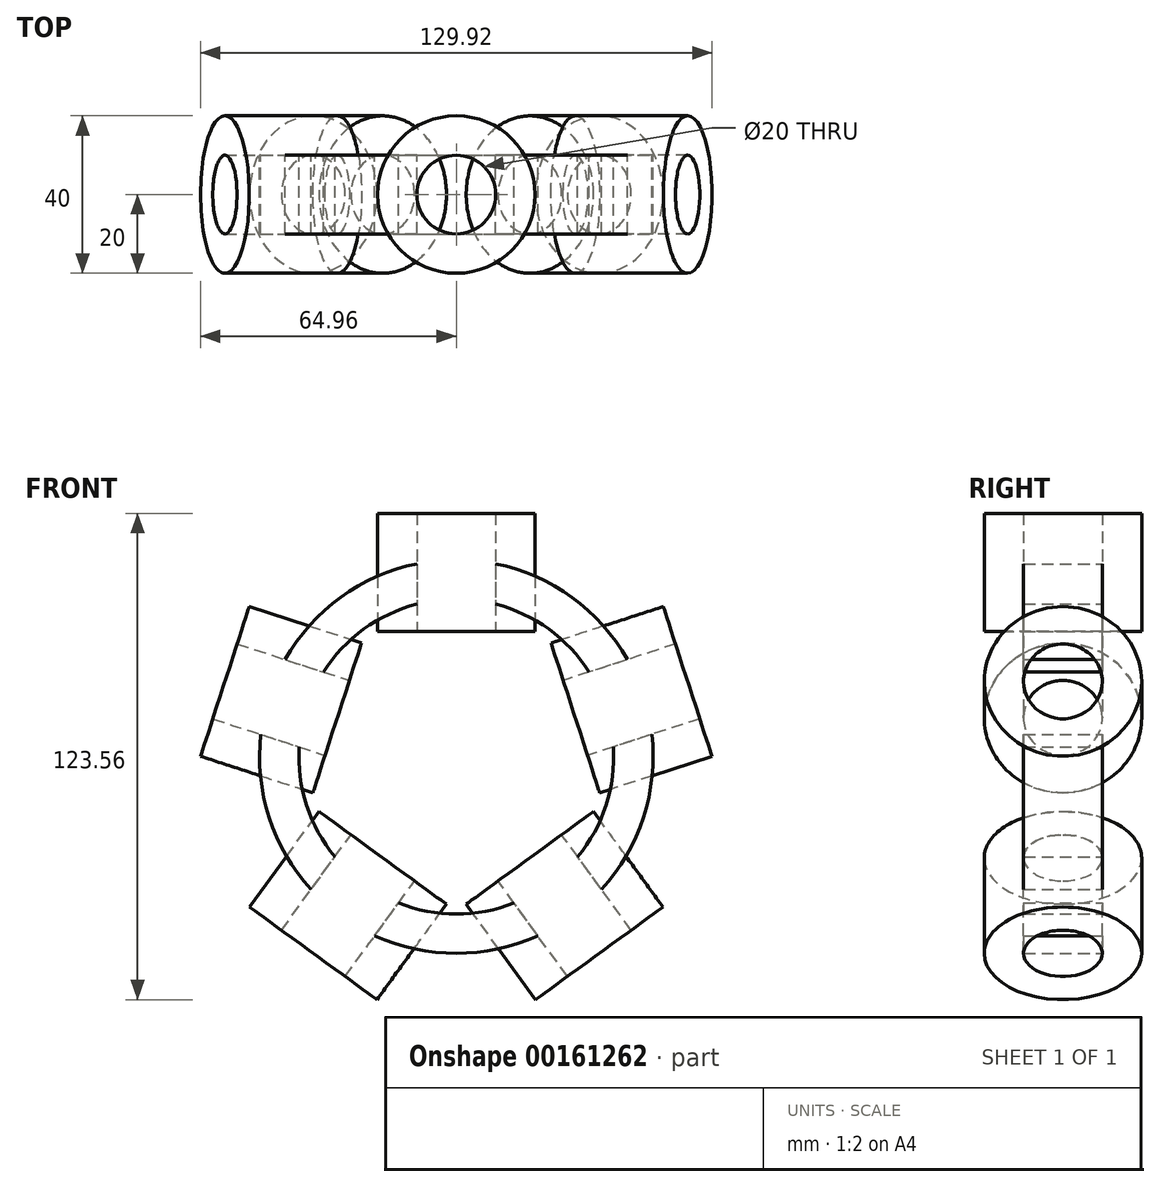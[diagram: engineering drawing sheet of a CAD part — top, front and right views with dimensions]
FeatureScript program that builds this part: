
annotation { "Feature Type Name" : "Feature", "Feature Type Description" : "" }
export const myFeature = defineFeature(function(context is Context, id is Id, definition is map)
    precondition{}
    {
        {
            var Q0;
            Q0=qCreatedBy(makeId("Front.planeOp"),FACE);
            var sketch = newSketch(context, id + "F0", { "sketchPlane" : qUnion([Q0])});
            skCircle(sketch, "E0.cCircle", {"center": v(0, 0) * mm, "radius": 50 * mm, "construction": true});
            skLineSegment(sketch, "E0.0", {"start": v(0, 61.8) * mm, "end": v(58.78, 19.1) * mm});
            skLineSegment(sketch, "E0.1", {"start": v(58.78, 19.1) * mm, "end": v(36.33, -50) * mm});
            skLineSegment(sketch, "E0.2", {"start": v(36.33, -50) * mm, "end": v(-36.33, -50) * mm});
            skLineSegment(sketch, "E0.3", {"start": v(-36.33, -50) * mm, "end": v(-58.78, 19.1) * mm});
            skLineSegment(sketch, "E0.4", {"start": v(-58.78, 19.1) * mm, "end": v(0, 61.8) * mm});
            skPoint(sketch, "E0.0.midPoint", {"position": v(29.39, 40.45) * mm});
            skLineSegment(sketch, "E1", {"start": v(0, 61.8) * mm, "end": v(10, 61.8) * mm});
            skLineSegment(sketch, "E2", {"start": v(10, 61.8) * mm, "end": v(10, 31.8) * mm});
            skLineSegment(sketch, "E3", {"start": v(10, 31.8) * mm, "end": v(20, 31.8) * mm});
            skLineSegment(sketch, "E4", {"start": v(20, 31.8) * mm, "end": v(20, 61.8) * mm});
            skLineSegment(sketch, "E5", {"start": v(20, 61.8) * mm, "end": v(10, 61.8) * mm});
            skCircle(sketch, "E6", {"center": v(0, 0) * mm, "radius": 50 * mm});
            skCircle(sketch, "E7.0", {"center": v(0, 0) * mm, "radius": 40 * mm});
            skLineSegment(sketch, "E8", {"start": v(0, 0) * mm, "end": v(0, 61.8) * mm, "construction": true});
            skLineSegment(sketch, "E9.MirrorCS", {"start": v(0, 61.8) * mm, "end": v(-10, 61.8) * mm});
            skLineSegment(sketch, "E10.MirrorCS", {"start": v(-10, 61.8) * mm, "end": v(-10, 31.8) * mm});
            skLineSegment(sketch, "E11.MirrorCS", {"start": v(-20, 61.8) * mm, "end": v(-10, 61.8) * mm});
            skLineSegment(sketch, "E12.MirrorCS", {"start": v(-20, 31.8) * mm, "end": v(-20, 61.8) * mm});
            skLineSegment(sketch, "E13.MirrorCS", {"start": v(-10, 31.8) * mm, "end": v(-20, 31.8) * mm});
            skLineSegment(sketch, "E14.1.0", {"start": v(-52.6, 38.12) * mm, "end": v(-55.69, 28.6) * mm});
            skLineSegment(sketch, "E14.1.1", {"start": v(-24.07, 28.85) * mm, "end": v(-52.6, 38.12) * mm});
            skLineSegment(sketch, "E14.1.2", {"start": v(-55.69, 28.6) * mm, "end": v(-27.16, 19.34) * mm});
            skLineSegment(sketch, "E14.1.3", {"start": v(-27.16, 19.34) * mm, "end": v(-24.07, 28.85) * mm});
            skLineSegment(sketch, "E14.1.4", {"start": v(-58.78, 19.1) * mm, "end": v(-55.69, 28.6) * mm});
            skLineSegment(sketch, "E14.1.5", {"start": v(-58.78, 19.1) * mm, "end": v(-61.87, 9.59) * mm});
            skLineSegment(sketch, "E14.1.6", {"start": v(-64.96, 0.08) * mm, "end": v(-61.87, 9.59) * mm});
            skLineSegment(sketch, "E14.1.7", {"start": v(-36.43, -9.2) * mm, "end": v(-64.96, 0.08) * mm});
            skLineSegment(sketch, "E14.1.8", {"start": v(-61.87, 9.59) * mm, "end": v(-33.34, 0.32) * mm});
            skLineSegment(sketch, "E14.1.9", {"start": v(-33.34, 0.32) * mm, "end": v(-36.43, -9.2) * mm});
            skLineSegment(sketch, "E14.1.10", {"start": v(0, 0) * mm, "end": v(-58.78, 19.1) * mm, "construction": true});
            skLineSegment(sketch, "E14.2.0", {"start": v(-52.5, -38.24) * mm, "end": v(-44.42, -44.12) * mm});
            skLineSegment(sketch, "E14.2.1", {"start": v(-34.87, -13.97) * mm, "end": v(-52.5, -38.24) * mm});
            skLineSegment(sketch, "E14.2.2", {"start": v(-44.42, -44.12) * mm, "end": v(-26.78, -19.85) * mm});
            skLineSegment(sketch, "E14.2.3", {"start": v(-26.78, -19.85) * mm, "end": v(-34.87, -13.97) * mm});
            skLineSegment(sketch, "E14.2.4", {"start": v(-36.33, -50) * mm, "end": v(-44.42, -44.12) * mm});
            skLineSegment(sketch, "E14.2.5", {"start": v(-36.33, -50) * mm, "end": v(-28.24, -55.88) * mm});
            skLineSegment(sketch, "E14.2.6", {"start": v(-20.15, -61.76) * mm, "end": v(-28.24, -55.88) * mm});
            skLineSegment(sketch, "E14.2.7", {"start": v(-2.51, -37.49) * mm, "end": v(-20.15, -61.76) * mm});
            skLineSegment(sketch, "E14.2.8", {"start": v(-28.24, -55.88) * mm, "end": v(-10.6, -31.6) * mm});
            skLineSegment(sketch, "E14.2.9", {"start": v(-10.6, -31.6) * mm, "end": v(-2.51, -37.49) * mm});
            skLineSegment(sketch, "E14.2.10", {"start": v(0, 0) * mm, "end": v(-36.33, -50) * mm, "construction": true});
            skLineSegment(sketch, "E14.3.0", {"start": v(20.15, -61.76) * mm, "end": v(28.24, -55.88) * mm});
            skLineSegment(sketch, "E14.3.1", {"start": v(2.51, -37.49) * mm, "end": v(20.15, -61.76) * mm});
            skLineSegment(sketch, "E14.3.2", {"start": v(28.24, -55.88) * mm, "end": v(10.6, -31.6) * mm});
            skLineSegment(sketch, "E14.3.3", {"start": v(10.6, -31.6) * mm, "end": v(2.51, -37.49) * mm});
            skLineSegment(sketch, "E14.3.4", {"start": v(36.33, -50) * mm, "end": v(28.24, -55.88) * mm});
            skLineSegment(sketch, "E14.3.5", {"start": v(36.33, -50) * mm, "end": v(44.42, -44.12) * mm});
            skLineSegment(sketch, "E14.3.6", {"start": v(52.5, -38.24) * mm, "end": v(44.42, -44.12) * mm});
            skLineSegment(sketch, "E14.3.7", {"start": v(34.87, -13.97) * mm, "end": v(52.5, -38.24) * mm});
            skLineSegment(sketch, "E14.3.8", {"start": v(44.42, -44.12) * mm, "end": v(26.78, -19.85) * mm});
            skLineSegment(sketch, "E14.3.9", {"start": v(26.78, -19.85) * mm, "end": v(34.87, -13.97) * mm});
            skLineSegment(sketch, "E14.3.10", {"start": v(0, 0) * mm, "end": v(36.33, -50) * mm, "construction": true});
            skLineSegment(sketch, "E14.4.0", {"start": v(64.96, 0.08) * mm, "end": v(61.87, 9.59) * mm});
            skLineSegment(sketch, "E14.4.1", {"start": v(36.43, -9.2) * mm, "end": v(64.96, 0.08) * mm});
            skLineSegment(sketch, "E14.4.2", {"start": v(61.87, 9.59) * mm, "end": v(33.34, 0.32) * mm});
            skLineSegment(sketch, "E14.4.3", {"start": v(33.34, 0.32) * mm, "end": v(36.43, -9.2) * mm});
            skLineSegment(sketch, "E14.4.4", {"start": v(58.78, 19.1) * mm, "end": v(61.87, 9.59) * mm});
            skLineSegment(sketch, "E14.4.5", {"start": v(58.78, 19.1) * mm, "end": v(55.69, 28.6) * mm});
            skLineSegment(sketch, "E14.4.6", {"start": v(52.6, 38.12) * mm, "end": v(55.69, 28.6) * mm});
            skLineSegment(sketch, "E14.4.7", {"start": v(24.07, 28.85) * mm, "end": v(52.6, 38.12) * mm});
            skLineSegment(sketch, "E14.4.8", {"start": v(55.69, 28.6) * mm, "end": v(27.16, 19.34) * mm});
            skLineSegment(sketch, "E14.4.9", {"start": v(27.16, 19.34) * mm, "end": v(24.07, 28.85) * mm});
            skLineSegment(sketch, "E14.4.10", {"start": v(0, 0) * mm, "end": v(58.78, 19.1) * mm, "construction": true});
            skSolve(sketch);
        }
        {
            var Q0;
            {var subQ5=sQuery(id+"F0.wireOp",EDGE,"E5");Q0=makeQuery(id+"F0.imprint","IMPRINT",FACE,{"disambiguationData":[TD([[makeQuery(id+"F0.imprint","IMPRINT",EDGE,{"derivedFrom":subQ5}),1.0]])]});}
            var Q1;
            {var subQ0=sQuery(id+"F0.wireOp",EDGE,"E4");var subQ1=sQuery(id+"F0.wireOp",EDGE,"E0.0");var subQ2=makeQuery(id+"F0.imprint","INTERSECT",VERTEX,{"derivedFrom":[subQ1,subQ0]});Q1=makeQuery(id+"F0.imprint","IMPRINT",FACE,{"disambiguationData":[TD([[makeQuery(id+"F0.imprint","IMPRINT",EDGE,{"disambiguationData":[TD([[subQ2,1.0]])],"derivedFrom":subQ1}),-1.0]])]});}
            var Q2;
            {var subQ0=sQuery(id+"F0.wireOp",EDGE,"E6");var subQ1=sQuery(id+"F0.wireOp",EDGE,"E2");var subQ2=makeQuery(id+"F0.imprint","INTERSECT",VERTEX,{"derivedFrom":[subQ1,subQ0]});Q2=makeQuery(id+"F0.imprint","IMPRINT",FACE,{"disambiguationData":[TD([[makeQuery(id+"F0.imprint","IMPRINT",EDGE,{"disambiguationData":[TD([[subQ2,-1.0]])],"derivedFrom":subQ1}),1.0]])]});}
            var Q3;
            {var subQ0=sQuery(id+"F0.wireOp",EDGE,"E3");Q3=makeQuery(id+"F0.imprint","IMPRINT",FACE,{"disambiguationData":[TD([[makeQuery(id+"F0.imprint","IMPRINT",EDGE,{"derivedFrom":subQ0}),1.0]])]});}
            var Q4;
            Q4=sQuery(id+"F0.wireOp",EDGE,"E8");
            revolve(context, id + "F1", {"entities" : qUnion([Q0, Q1, Q2, Q3]), "axis" : qUnion([Q4]), "revolveType" : RevolveType.FULL});
        }
        {
            var Q0;
            {var subQ5=sQuery(id+"F0.wireOp",EDGE,"E14.4.0");Q0=makeQuery(id+"F0.imprint","IMPRINT",FACE,{"disambiguationData":[TD([[makeQuery(id+"F0.imprint","IMPRINT",EDGE,{"derivedFrom":subQ5}),1.0]])]});}
            var Q1;
            {var subQ0=sQuery(id+"F0.wireOp",EDGE,"E14.4.1");var subQ1=sQuery(id+"F0.wireOp",EDGE,"E0.1");var subQ2=makeQuery(id+"F0.imprint","INTERSECT",VERTEX,{"derivedFrom":[subQ1,subQ0]});Q1=makeQuery(id+"F0.imprint","IMPRINT",FACE,{"disambiguationData":[TD([[makeQuery(id+"F0.imprint","IMPRINT",EDGE,{"disambiguationData":[TD([[subQ2,1.0]])],"derivedFrom":subQ1}),-1.0]])]});}
            var Q2;
            {var subQ0=sQuery(id+"F0.wireOp",EDGE,"E14.4.2");var subQ1=sQuery(id+"F0.wireOp",EDGE,"E6");var subQ2=makeQuery(id+"F0.imprint","INTERSECT",VERTEX,{"derivedFrom":[subQ1,subQ0]});Q2=makeQuery(id+"F0.imprint","IMPRINT",FACE,{"disambiguationData":[TD([[makeQuery(id+"F0.imprint","IMPRINT",EDGE,{"disambiguationData":[TD([[subQ2,1.0]])],"derivedFrom":subQ1}),1.0]])]});}
            var Q3;
            {var subQ5=sQuery(id+"F0.wireOp",EDGE,"E14.4.3");Q3=makeQuery(id+"F0.imprint","IMPRINT",FACE,{"disambiguationData":[TD([[makeQuery(id+"F0.imprint","IMPRINT",EDGE,{"derivedFrom":subQ5}),1.0]])]});}
            var Q4;
            Q4=sQuery(id+"F0.wireOp",EDGE,"E14.4.10");
            revolve(context, id + "F2", {"entities" : qUnion([Q0, Q1, Q2, Q3]), "axis" : qUnion([Q4]), "revolveType" : RevolveType.FULL});
        }
        {
            var Q0;
            {var subQ5=sQuery(id+"F0.wireOp",EDGE,"E14.3.0");Q0=makeQuery(id+"F0.imprint","IMPRINT",FACE,{"disambiguationData":[TD([[makeQuery(id+"F0.imprint","IMPRINT",EDGE,{"derivedFrom":subQ5}),1.0]])]});}
            var Q1;
            {var subQ0=sQuery(id+"F0.wireOp",EDGE,"E14.3.1");var subQ1=sQuery(id+"F0.wireOp",EDGE,"E0.2");var subQ2=makeQuery(id+"F0.imprint","INTERSECT",VERTEX,{"derivedFrom":[subQ1,subQ0]});Q1=makeQuery(id+"F0.imprint","IMPRINT",FACE,{"disambiguationData":[TD([[makeQuery(id+"F0.imprint","IMPRINT",EDGE,{"disambiguationData":[TD([[subQ2,1.0]])],"derivedFrom":subQ1}),-1.0]])]});}
            var Q2;
            {var subQ0=sQuery(id+"F0.wireOp",EDGE,"E14.3.1");var subQ1=sQuery(id+"F0.wireOp",EDGE,"E6");var subQ2=makeQuery(id+"F0.imprint","INTERSECT",VERTEX,{"derivedFrom":[subQ1,subQ0]});Q2=makeQuery(id+"F0.imprint","IMPRINT",FACE,{"disambiguationData":[TD([[makeQuery(id+"F0.imprint","IMPRINT",EDGE,{"disambiguationData":[TD([[subQ2,-1.0]])],"derivedFrom":subQ1}),1.0]])]});}
            var Q3;
            {var subQ5=sQuery(id+"F0.wireOp",EDGE,"E14.3.3");Q3=makeQuery(id+"F0.imprint","IMPRINT",FACE,{"disambiguationData":[TD([[makeQuery(id+"F0.imprint","IMPRINT",EDGE,{"derivedFrom":subQ5}),1.0]])]});}
            var Q4;
            Q4=sQuery(id+"F0.wireOp",EDGE,"E14.3.10");
            revolve(context, id + "F3", {"entities" : qUnion([Q0, Q1, Q2, Q3]), "axis" : qUnion([Q4]), "revolveType" : RevolveType.FULL});
        }
        {
            var Q0;
            {var subQ0=sQuery(id+"F0.wireOp",EDGE,"E14.2.1");var subQ1=sQuery(id+"F0.wireOp",EDGE,"E6");var subQ2=makeQuery(id+"F0.imprint","INTERSECT",VERTEX,{"derivedFrom":[subQ1,subQ0]});Q0=makeQuery(id+"F0.imprint","IMPRINT",FACE,{"disambiguationData":[TD([[makeQuery(id+"F0.imprint","IMPRINT",EDGE,{"disambiguationData":[TD([[subQ2,-1.0]])],"derivedFrom":subQ1}),1.0]])]});}
            var Q1;
            {var subQ5=sQuery(id+"F0.wireOp",EDGE,"E14.2.3");Q1=makeQuery(id+"F0.imprint","IMPRINT",FACE,{"disambiguationData":[TD([[makeQuery(id+"F0.imprint","IMPRINT",EDGE,{"derivedFrom":subQ5}),1.0]])]});}
            var Q2;
            {var subQ0=sQuery(id+"F0.wireOp",EDGE,"E14.2.1");var subQ1=sQuery(id+"F0.wireOp",EDGE,"E0.3");var subQ2=makeQuery(id+"F0.imprint","INTERSECT",VERTEX,{"derivedFrom":[subQ1,subQ0]});Q2=makeQuery(id+"F0.imprint","IMPRINT",FACE,{"disambiguationData":[TD([[makeQuery(id+"F0.imprint","IMPRINT",EDGE,{"disambiguationData":[TD([[subQ2,1.0]])],"derivedFrom":subQ1}),-1.0]])]});}
            var Q3;
            {var subQ5=sQuery(id+"F0.wireOp",EDGE,"E14.2.0");Q3=makeQuery(id+"F0.imprint","IMPRINT",FACE,{"disambiguationData":[TD([[makeQuery(id+"F0.imprint","IMPRINT",EDGE,{"derivedFrom":subQ5}),1.0]])]});}
            var Q4;
            Q4=sQuery(id+"F0.wireOp",EDGE,"E14.2.10");
            revolve(context, id + "F4", {"entities" : qUnion([Q0, Q1, Q2, Q3]), "axis" : qUnion([Q4]), "revolveType" : RevolveType.FULL});
        }
        {
            var Q0;
            {var subQ5=sQuery(id+"F0.wireOp",EDGE,"E14.1.0");Q0=makeQuery(id+"F0.imprint","IMPRINT",FACE,{"disambiguationData":[TD([[makeQuery(id+"F0.imprint","IMPRINT",EDGE,{"derivedFrom":subQ5}),1.0]])]});}
            var Q1;
            {var subQ0=sQuery(id+"F0.wireOp",EDGE,"E14.1.1");var subQ1=sQuery(id+"F0.wireOp",EDGE,"E0.4");var subQ2=makeQuery(id+"F0.imprint","INTERSECT",VERTEX,{"derivedFrom":[subQ1,subQ0]});Q1=makeQuery(id+"F0.imprint","IMPRINT",FACE,{"disambiguationData":[TD([[makeQuery(id+"F0.imprint","IMPRINT",EDGE,{"disambiguationData":[TD([[subQ2,1.0]])],"derivedFrom":subQ1}),-1.0]])]});}
            var Q2;
            {var subQ0=sQuery(id+"F0.wireOp",EDGE,"E14.1.1");var subQ1=sQuery(id+"F0.wireOp",EDGE,"E6");var subQ2=makeQuery(id+"F0.imprint","INTERSECT",VERTEX,{"derivedFrom":[subQ1,subQ0]});Q2=makeQuery(id+"F0.imprint","IMPRINT",FACE,{"disambiguationData":[TD([[makeQuery(id+"F0.imprint","IMPRINT",EDGE,{"disambiguationData":[TD([[subQ2,-1.0]])],"derivedFrom":subQ1}),1.0]])]});}
            var Q3;
            {var subQ5=sQuery(id+"F0.wireOp",EDGE,"E14.1.3");Q3=makeQuery(id+"F0.imprint","IMPRINT",FACE,{"disambiguationData":[TD([[makeQuery(id+"F0.imprint","IMPRINT",EDGE,{"derivedFrom":subQ5}),1.0]])]});}
            var Q4;
            Q4=sQuery(id+"F0.wireOp",EDGE,"E14.1.10");
            revolve(context, id + "F5", {"entities" : qUnion([Q0, Q1, Q2, Q3]), "axis" : qUnion([Q4]), "revolveType" : RevolveType.FULL});
        }
        {
            var Q0;
            {var subQ1=sQuery(id+"F0.wireOp",EDGE,"E6");var subQ7=makeQuery(id+"F0.imprint","INTERSECT",VERTEX,{"derivedFrom":[sQuery(id+"F0.wireOp",EDGE,"E0.4"),subQ1]});Q0=makeQuery(id+"F0.imprint","IMPRINT",FACE,{"disambiguationData":[TD([[makeQuery(id+"F0.imprint","IMPRINT",EDGE,{"disambiguationData":[TD([[subQ7,1.0]])],"derivedFrom":subQ1}),1.0]])]});}
            var Q1;
            {var subQ2=sQuery(id+"F0.wireOp",EDGE,"E4");var subQ6=sQuery(id+"F0.wireOp",EDGE,"E7.0");var subQ7=makeQuery(id+"F0.imprint","INTERSECT",VERTEX,{"derivedFrom":[subQ2,subQ6]});Q1=makeQuery(id+"F0.imprint","IMPRINT",FACE,{"disambiguationData":[TD([[makeQuery(id+"F0.imprint","IMPRINT",EDGE,{"disambiguationData":[TD([[subQ7,-1.0]])],"derivedFrom":subQ2}),-1.0]])]});}
            var Q2;
            {var subQ1=sQuery(id+"F0.wireOp",EDGE,"E6");var subQ7=makeQuery(id+"F0.imprint","INTERSECT",VERTEX,{"derivedFrom":[sQuery(id+"F0.wireOp",EDGE,"E0.1"),subQ1]});Q2=makeQuery(id+"F0.imprint","IMPRINT",FACE,{"disambiguationData":[TD([[makeQuery(id+"F0.imprint","IMPRINT",EDGE,{"disambiguationData":[TD([[subQ7,1.0]])],"derivedFrom":subQ1}),1.0]])]});}
            var Q3;
            {var subQ1=sQuery(id+"F0.wireOp",EDGE,"E6");var subQ8=makeQuery(id+"F0.imprint","INTERSECT",VERTEX,{"derivedFrom":[sQuery(id+"F0.wireOp",EDGE,"E0.2"),subQ1]});Q3=makeQuery(id+"F0.imprint","IMPRINT",FACE,{"disambiguationData":[TD([[makeQuery(id+"F0.imprint","IMPRINT",EDGE,{"disambiguationData":[TD([[subQ8,1.0]])],"derivedFrom":subQ1}),1.0]])]});}
            var Q4;
            {var subQ1=sQuery(id+"F0.wireOp",EDGE,"E6");var subQ7=makeQuery(id+"F0.imprint","INTERSECT",VERTEX,{"derivedFrom":[sQuery(id+"F0.wireOp",EDGE,"E0.3"),subQ1]});Q4=makeQuery(id+"F0.imprint","IMPRINT",FACE,{"disambiguationData":[TD([[makeQuery(id+"F0.imprint","IMPRINT",EDGE,{"disambiguationData":[TD([[subQ7,1.0]])],"derivedFrom":subQ1}),1.0]])]});}
            var Q5;
            {var subQ0=sQuery(id+"F0.wireOp",EDGE,"E14.1.8");var subQ1=sQuery(id+"F0.wireOp",EDGE,"E6");var subQ2=makeQuery(id+"F0.imprint","INTERSECT",VERTEX,{"derivedFrom":[subQ1,subQ0]});Q5=makeQuery(id+"F0.imprint","IMPRINT",FACE,{"disambiguationData":[TD([[makeQuery(id+"F0.imprint","IMPRINT",EDGE,{"disambiguationData":[TD([[subQ2,-1.0]])],"derivedFrom":subQ1}),1.0]])]});}
            var Q6;
            {var subQ0=sQuery(id+"F0.wireOp",EDGE,"E14.2.1");var subQ1=sQuery(id+"F0.wireOp",EDGE,"E6");var subQ2=makeQuery(id+"F0.imprint","INTERSECT",VERTEX,{"derivedFrom":[subQ1,subQ0]});Q6=makeQuery(id+"F0.imprint","IMPRINT",FACE,{"disambiguationData":[TD([[makeQuery(id+"F0.imprint","IMPRINT",EDGE,{"disambiguationData":[TD([[subQ2,-1.0]])],"derivedFrom":subQ1}),1.0]])]});}
            var Q7;
            {var subQ0=sQuery(id+"F0.wireOp",EDGE,"E14.2.8");var subQ1=sQuery(id+"F0.wireOp",EDGE,"E6");var subQ2=makeQuery(id+"F0.imprint","INTERSECT",VERTEX,{"derivedFrom":[subQ1,subQ0]});Q7=makeQuery(id+"F0.imprint","IMPRINT",FACE,{"disambiguationData":[TD([[makeQuery(id+"F0.imprint","IMPRINT",EDGE,{"disambiguationData":[TD([[subQ2,-1.0]])],"derivedFrom":subQ1}),1.0]])]});}
            var Q8;
            {var subQ0=sQuery(id+"F0.wireOp",EDGE,"E14.3.1");var subQ1=sQuery(id+"F0.wireOp",EDGE,"E6");var subQ2=makeQuery(id+"F0.imprint","INTERSECT",VERTEX,{"derivedFrom":[subQ1,subQ0]});Q8=makeQuery(id+"F0.imprint","IMPRINT",FACE,{"disambiguationData":[TD([[makeQuery(id+"F0.imprint","IMPRINT",EDGE,{"disambiguationData":[TD([[subQ2,-1.0]])],"derivedFrom":subQ1}),1.0]])]});}
            var Q9;
            {var subQ0=sQuery(id+"F0.wireOp",EDGE,"E14.3.8");var subQ1=sQuery(id+"F0.wireOp",EDGE,"E6");var subQ2=makeQuery(id+"F0.imprint","INTERSECT",VERTEX,{"derivedFrom":[subQ1,subQ0]});Q9=makeQuery(id+"F0.imprint","IMPRINT",FACE,{"disambiguationData":[TD([[makeQuery(id+"F0.imprint","IMPRINT",EDGE,{"disambiguationData":[TD([[subQ2,-1.0]])],"derivedFrom":subQ1}),1.0]])]});}
            var Q10;
            {var subQ0=sQuery(id+"F0.wireOp",EDGE,"E14.4.2");var subQ1=sQuery(id+"F0.wireOp",EDGE,"E6");var subQ2=makeQuery(id+"F0.imprint","INTERSECT",VERTEX,{"derivedFrom":[subQ1,subQ0]});Q10=makeQuery(id+"F0.imprint","IMPRINT",FACE,{"disambiguationData":[TD([[makeQuery(id+"F0.imprint","IMPRINT",EDGE,{"disambiguationData":[TD([[subQ2,1.0]])],"derivedFrom":subQ1}),1.0]])]});}
            var Q11;
            {var subQ0=sQuery(id+"F0.wireOp",EDGE,"E14.4.8");var subQ1=sQuery(id+"F0.wireOp",EDGE,"E6");var subQ2=makeQuery(id+"F0.imprint","INTERSECT",VERTEX,{"derivedFrom":[subQ1,subQ0]});Q11=makeQuery(id+"F0.imprint","IMPRINT",FACE,{"disambiguationData":[TD([[makeQuery(id+"F0.imprint","IMPRINT",EDGE,{"disambiguationData":[TD([[subQ2,-1.0]])],"derivedFrom":subQ1}),1.0]])]});}
            var Q12;
            {var subQ0=sQuery(id+"F0.wireOp",EDGE,"E6");var subQ1=sQuery(id+"F0.wireOp",EDGE,"E2");var subQ2=makeQuery(id+"F0.imprint","INTERSECT",VERTEX,{"derivedFrom":[subQ1,subQ0]});Q12=makeQuery(id+"F0.imprint","IMPRINT",FACE,{"disambiguationData":[TD([[makeQuery(id+"F0.imprint","IMPRINT",EDGE,{"disambiguationData":[TD([[subQ2,-1.0]])],"derivedFrom":subQ1}),1.0]])]});}
            var Q13;
            {var subQ0=sQuery(id+"F0.wireOp",EDGE,"E10.MirrorCS");var subQ1=sQuery(id+"F0.wireOp",EDGE,"E6");var subQ2=makeQuery(id+"F0.imprint","INTERSECT",VERTEX,{"derivedFrom":[subQ1,subQ0]});Q13=makeQuery(id+"F0.imprint","IMPRINT",FACE,{"disambiguationData":[TD([[makeQuery(id+"F0.imprint","IMPRINT",EDGE,{"disambiguationData":[TD([[subQ2,-1.0]])],"derivedFrom":subQ1}),1.0]])]});}
            var Q14;
            {var subQ0=sQuery(id+"F0.wireOp",EDGE,"E14.1.1");var subQ1=sQuery(id+"F0.wireOp",EDGE,"E6");var subQ2=makeQuery(id+"F0.imprint","INTERSECT",VERTEX,{"derivedFrom":[subQ1,subQ0]});Q14=makeQuery(id+"F0.imprint","IMPRINT",FACE,{"disambiguationData":[TD([[makeQuery(id+"F0.imprint","IMPRINT",EDGE,{"disambiguationData":[TD([[subQ2,-1.0]])],"derivedFrom":subQ1}),1.0]])]});}
            extrude(context, id + "F6", {"entities" : qUnion([Q0, Q1, Q2, Q3, Q4, Q5, Q6, Q7, Q8, Q9, Q10, Q11, Q12, Q13, Q14]), "depth" : 20 * mm, "symmetric" : true});
        }
    });
